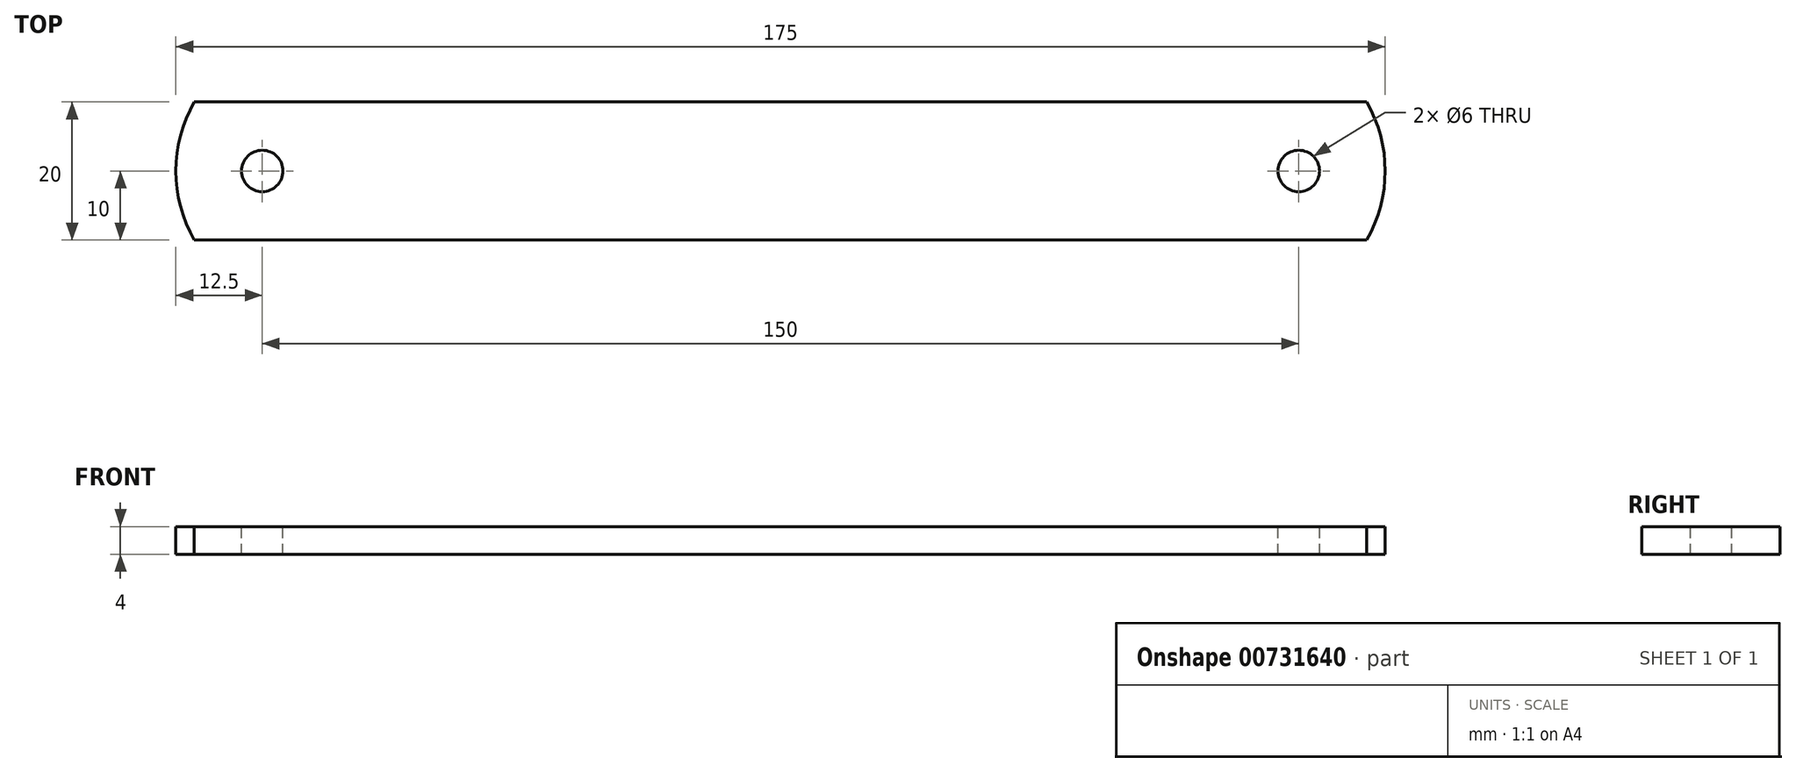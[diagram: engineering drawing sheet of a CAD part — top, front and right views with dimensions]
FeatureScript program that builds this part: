
annotation { "Feature Type Name" : "Feature", "Feature Type Description" : "" }
export const myFeature = defineFeature(function(context is Context, id is Id, definition is map)
    precondition{}
    {
        {
            var Q0;
            Q0=qCreatedBy(makeId("Top.planeOp"),FACE);
            var sketch = newSketch(context, id + "F0", { "sketchPlane" : qUnion([Q0])});
            skLineSegment(sketch, "E0.bottom", {"start": v(0, 0) * mm, "end": v(169.64, 0) * mm});
            skLineSegment(sketch, "E0.top", {"start": v(0, -20) * mm, "end": v(169.64, -20) * mm});
            skArc(sketch, "E1", {"start": v(169.64, -20) * mm, "mid": v(172.32, -10) * mm, "end": v(169.64, 0) * mm});
            skArc(sketch, "E2", {"start": v(0, 0) * mm, "mid": v(-2.68, -10) * mm, "end": v(0, -20) * mm});
            skSolve(sketch);
        }
        {
            var Q0;
            Q0=makeQuery(id+"F0.imprint","IMPRINT",FACE,{"disambiguationData":[TD([[makeQuery(id+"F0.imprint","IMPRINT",EDGE,{"derivedFrom":sQuery(id+"F0.wireOp",EDGE,"E0.bottom")}),-1.0]])]});
            extrude(context, id + "F1", {"entities" : qUnion([Q0]), "depth" : 4 * mm, "offsetDistance" : 25 * mm});
        }
        {
            var Q0;
            Q0=makeQuery(id+"F1.opExtrude","CAP_FACE",FACE,{"disambiguationData":[OSD([sQuery(id+"F0.wireOp",EDGE,"E0.bottom"),sQuery(id+"F0.wireOp",EDGE,"E0.top"),sQuery(id+"F0.wireOp",EDGE,"E1"),sQuery(id+"F0.wireOp",EDGE,"E2")])],"isStart":false});
            var sketch = newSketch(context, id + "F2", { "sketchPlane" : qUnion([Q0])});
            skCircle(sketch, "E3", {"center": v(159.82, -10) * mm, "radius": 3 * mm});
            skCircle(sketch, "E4", {"center": v(9.82, -10) * mm, "radius": 3 * mm});
            skSolve(sketch);
        }
        {
            var Q0;
            Q0 = qSketchRegion(id + "F2", true);
            extrude(context, id + "F3", {"entities" : qUnion([Q0]), "operationType" : NewBodyOperationType.REMOVE, "oppositeDirection" : true, "depth" : 4 * mm, "offsetDistance" : 25 * mm});
        }
    });
